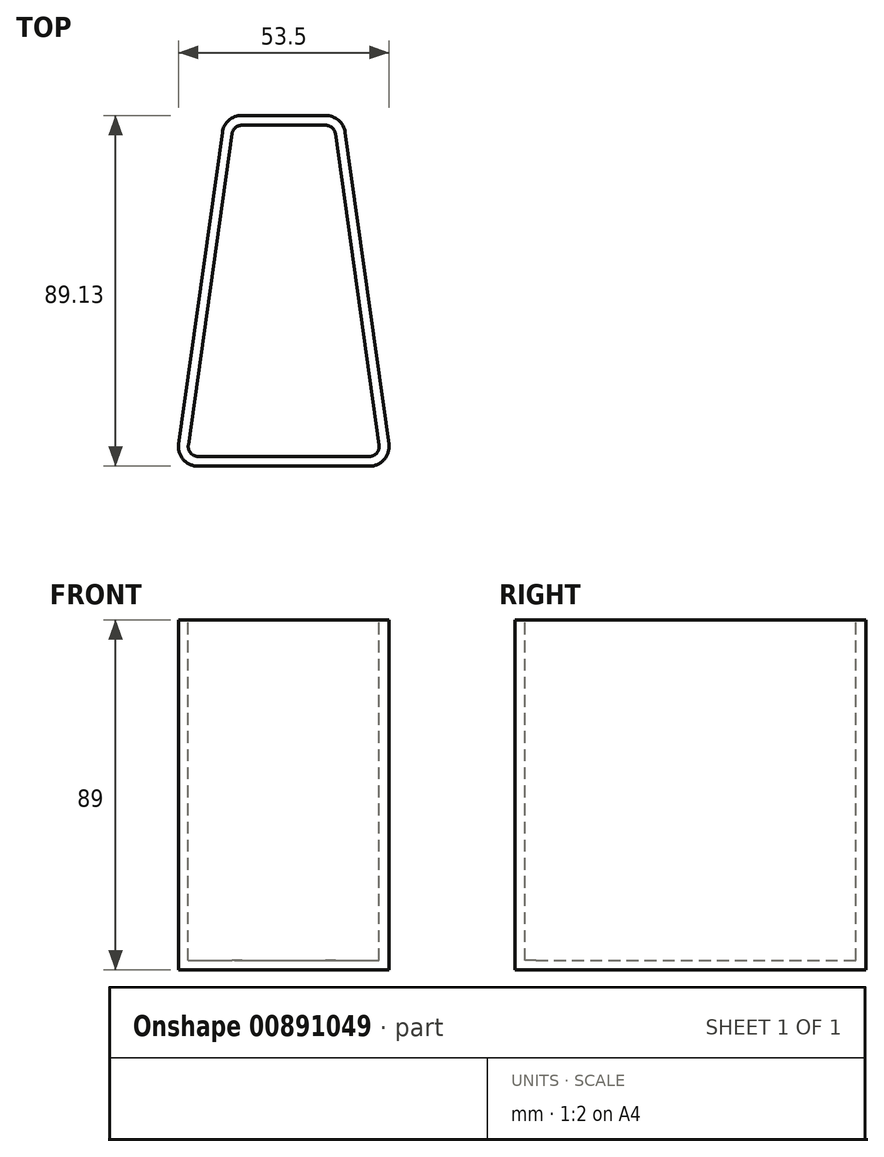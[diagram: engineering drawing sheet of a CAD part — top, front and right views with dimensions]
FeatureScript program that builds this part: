
annotation { "Feature Type Name" : "Feature", "Feature Type Description" : "" }
export const myFeature = defineFeature(function(context is Context, id is Id, definition is map)
    precondition{}
    {
        {
            var Q0;
            Q0=qCreatedBy(makeId("Top.planeOp"),FACE);
            var sketch = newSketch(context, id + "F0", { "sketchPlane" : qUnion([Q0])});
            skLineSegment(sketch, "E0", {"start": v(-34.44, -16.18) * mm, "end": v(20.56, -16.18) * mm});
            skLineSegment(sketch, "E1", {"start": v(-21.94, 72.95) * mm, "end": v(8.06, 72.95) * mm});
            skLineSegment(sketch, "E2", {"start": v(-6.94, -16.18) * mm, "end": v(-6.94, 72.95) * mm, "construction": true});
            skLineSegment(sketch, "E3", {"start": v(-34.44, -16.18) * mm, "end": v(-21.94, 72.95) * mm});
            skLineSegment(sketch, "E4", {"start": v(8.06, 72.95) * mm, "end": v(20.56, -16.18) * mm});
            skSolve(sketch);
        }
        {
            var Q0;
            Q0=makeQuery(id+"F0.imprint","IMPRINT",FACE,{"disambiguationData":[TD([[makeQuery(id+"F0.imprint","IMPRINT",EDGE,{"derivedFrom":sQuery(id+"F0.wireOp",EDGE,"E0")}),1.0]])]});
            extrude(context, id + "F1", {"entities" : qUnion([Q0]), "depth" : 89 * mm, "offsetDistance" : 25 * mm});
        }
        {
            var Q0;
            Q0=makeQuery(id+"F1.opExtrude","SWEPT_EDGE",EDGE,{"disambiguationData":[OSD([sQuery(id+"F0.wireOp",EDGE,"E0"),sQuery(id+"F0.wireOp",EDGE,"E3")])]});
            var Q1;
            Q1=makeQuery(id+"F1.opExtrude","SWEPT_EDGE",EDGE,{"disambiguationData":[OSD([sQuery(id+"F0.wireOp",EDGE,"E0"),sQuery(id+"F0.wireOp",EDGE,"E4")])]});
            var Q2;
            Q2=makeQuery(id+"F1.opExtrude","SWEPT_EDGE",EDGE,{"disambiguationData":[OSD([sQuery(id+"F0.wireOp",EDGE,"E1"),sQuery(id+"F0.wireOp",EDGE,"E4")])]});
            var Q3;
            Q3=makeQuery(id+"F1.opExtrude","SWEPT_EDGE",EDGE,{"disambiguationData":[OSD([sQuery(id+"F0.wireOp",EDGE,"E1"),sQuery(id+"F0.wireOp",EDGE,"E3")])]});
            fillet(context, id + "F2", {"entities" : qUnion([Q0, Q1, Q2, Q3]), "radius" : 5 * mm, "tangentPropagation" : true, "allowEdgeOverflow" : false});
        }
        {
            var Q0;
            Q0=makeQuery(id+"F1.opExtrude","CAP_FACE",FACE,{"disambiguationData":[OSD([sQuery(id+"F0.wireOp",EDGE,"E0"),sQuery(id+"F0.wireOp",EDGE,"E1"),sQuery(id+"F0.wireOp",EDGE,"E3"),sQuery(id+"F0.wireOp",EDGE,"E4")])],"isStart":false});
            shell(context, id + "F3", {"entities" : qUnion([Q0]), "thickness" : 2.5 * mm});
        }
    });
